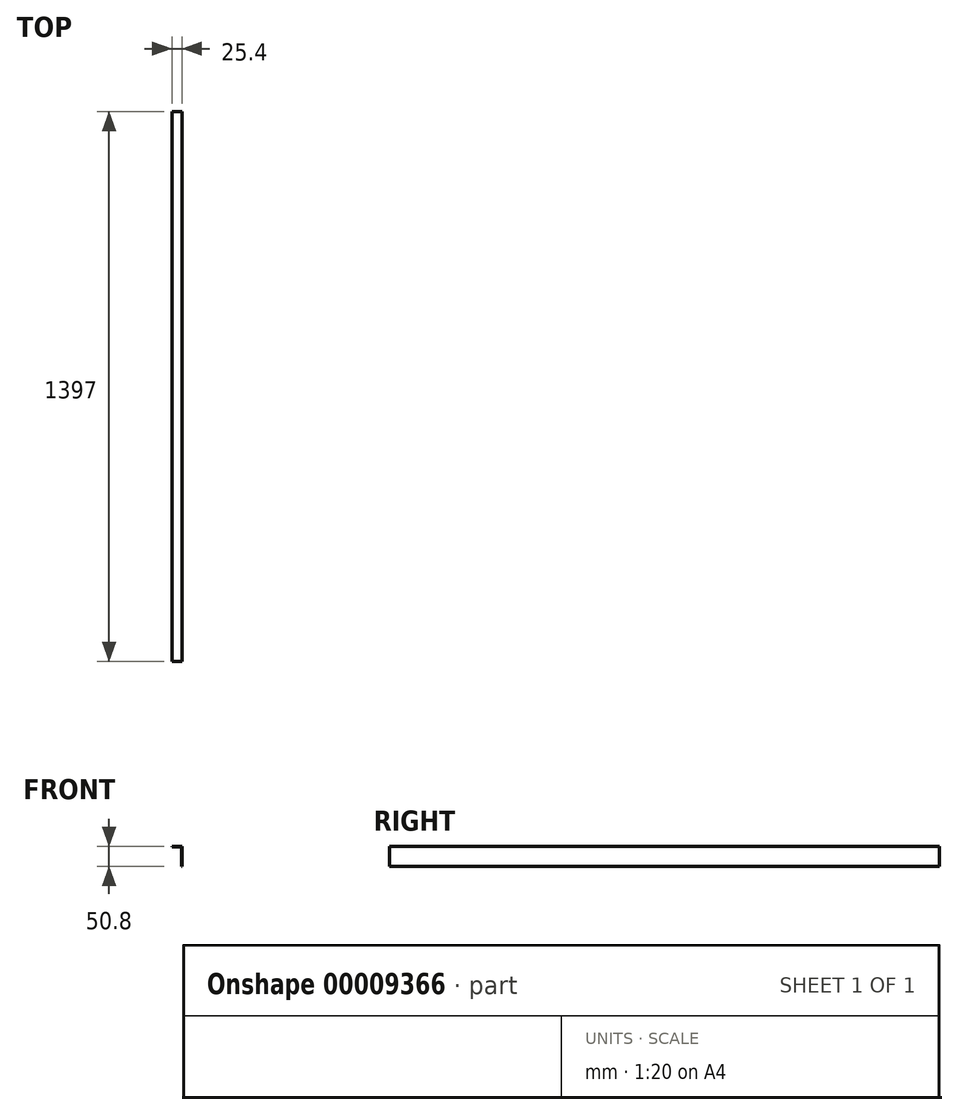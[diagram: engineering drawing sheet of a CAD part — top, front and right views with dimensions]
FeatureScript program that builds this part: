
annotation { "Feature Type Name" : "Feature", "Feature Type Description" : "" }
export const myFeature = defineFeature(function(context is Context, id is Id, definition is map)
    precondition{}
    {
        {
            var Q0;
            Q0=qCreatedBy(makeId("Front.planeOp"),FACE);
            var sketch = newSketch(context, id + "F0", { "sketchPlane" : qUnion([Q0])});
            skLineSegment(sketch, "E0", {"start": v(-2.03, -46.54) * mm, "end": v(-2.03, 2.95) * mm});
            skLineSegment(sketch, "E1", {"start": v(-2.03, 2.95) * mm, "end": v(-26.12, 2.95) * mm});
            skLineSegment(sketch, "E2", {"start": v(-26.12, 2.95) * mm, "end": v(-26.12, 4.26) * mm});
            skLineSegment(sketch, "E3", {"start": v(-26.12, 4.26) * mm, "end": v(-0.72, 4.26) * mm});
            skLineSegment(sketch, "E4", {"start": v(-0.72, 4.26) * mm, "end": v(-0.72, -46.54) * mm});
            skLineSegment(sketch, "E5", {"start": v(-0.72, -46.54) * mm, "end": v(-2.03, -46.54) * mm});
            skSolve(sketch);
        }
        {
            var Q0;
            Q0=makeQuery(id+"F0.imprint","IMPRINT",FACE,{"disambiguationData":[TD([[makeQuery(id+"F0.imprint","IMPRINT",EDGE,{"derivedFrom":sQuery(id+"F0.wireOp",EDGE,"E0")}),-1.0]])]});
            extrude(context, id + "F1", {"entities" : qUnion([Q0]), "depth" : 1397 * mm});
        }
    });
